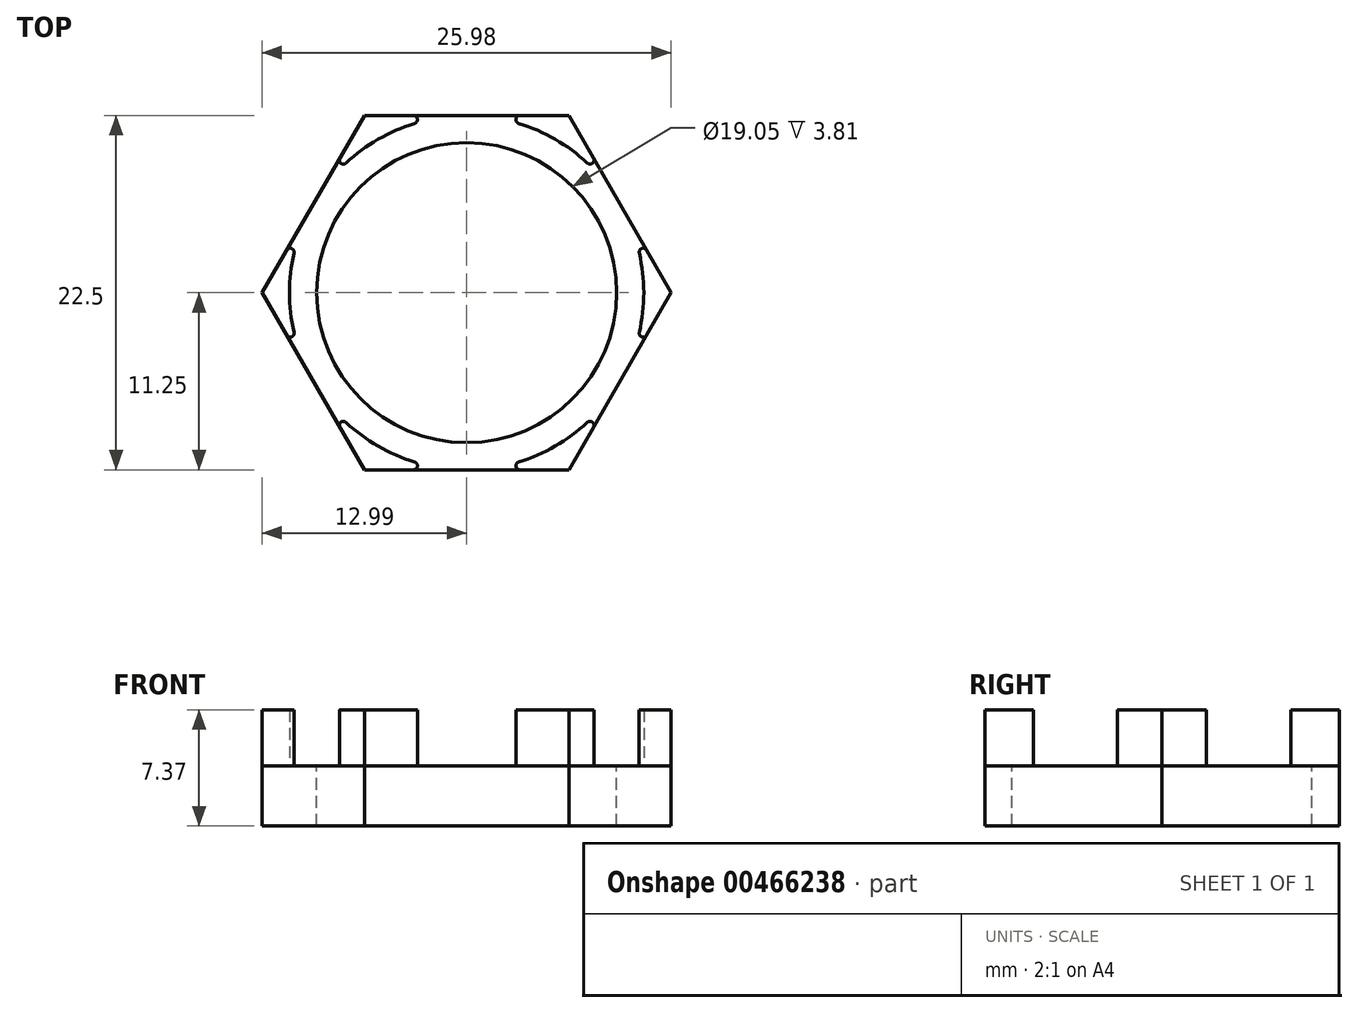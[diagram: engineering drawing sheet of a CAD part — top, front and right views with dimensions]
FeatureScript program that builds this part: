
annotation { "Feature Type Name" : "Feature", "Feature Type Description" : "" }
export const myFeature = defineFeature(function(context is Context, id is Id, definition is map)
    precondition{}
    {
        {
            var Q0;
            Q0=qCreatedBy(makeId("Top.planeOp"),FACE);
            var sketch = newSketch(context, id + "F0", { "sketchPlane" : qUnion([Q0])});
            skCircle(sketch, "E0.cCircle", {"center": v(0, 0) * mm, "radius": 11.25 * mm, "construction": true});
            skLineSegment(sketch, "E0.0", {"start": v(-6.5, 11.25) * mm, "end": v(6.5, 11.25) * mm});
            skLineSegment(sketch, "E0.1", {"start": v(6.5, 11.25) * mm, "end": v(13, 0) * mm});
            skLineSegment(sketch, "E0.2", {"start": v(13, 0) * mm, "end": v(6.5, -11.25) * mm});
            skLineSegment(sketch, "E0.3", {"start": v(6.5, -11.25) * mm, "end": v(-6.5, -11.25) * mm});
            skLineSegment(sketch, "E0.4", {"start": v(-6.5, -11.25) * mm, "end": v(-13, 0) * mm});
            skLineSegment(sketch, "E0.5", {"start": v(-13, 0) * mm, "end": v(-6.5, 11.25) * mm});
            skPoint(sketch, "E0.0.midPoint", {"position": v(0, 11.25) * mm});
            skSolve(sketch);
        }
        {
            var Q0;
            Q0=makeQuery(id+"F0.imprint","IMPRINT",FACE,{"disambiguationData":[TD([[makeQuery(id+"F0.imprint","IMPRINT",EDGE,{"derivedFrom":sQuery(id+"F0.wireOp",EDGE,"E0.0")}),-1.0]])]});
            extrude(context, id + "F1", {"entities" : qUnion([Q0]), "depth" : 3.8 * mm});
        }
        {
            var Q0;
            Q0=makeQuery(id+"F1.opExtrude","CAP_FACE",FACE,{"disambiguationData":[OSD([sQuery(id+"F0.wireOp",EDGE,"E0.0"),sQuery(id+"F0.wireOp",EDGE,"E0.1"),sQuery(id+"F0.wireOp",EDGE,"E0.2"),sQuery(id+"F0.wireOp",EDGE,"E0.3"),sQuery(id+"F0.wireOp",EDGE,"E0.4"),sQuery(id+"F0.wireOp",EDGE,"E0.5")])],"isStart":false});
            var sketch = newSketch(context, id + "F2", { "sketchPlane" : qUnion([Q0])});
            skCircle(sketch, "E1.cCircle", {"center": v(0, 0) * mm, "radius": 11.25 * mm, "construction": true});
            skLineSegment(sketch, "E1.0", {"start": v(9.74, 5.62) * mm, "end": v(13, 0) * mm});
            skLineSegment(sketch, "E1.1", {"start": v(13, 0) * mm, "end": v(9.74, -5.62) * mm});
            skPoint(sketch, "E1.0.midPoint", {"position": v(9.74, 5.62) * mm});
            skArc(sketch, "E2", {"start": v(9.74, -5.62) * mm, "mid": v(11.25, 0) * mm, "end": v(9.74, 5.62) * mm});
            skPoint(sketch, "E3.orphan", {"position": v(6.5, 11.25) * mm});
            skSolve(sketch);
        }
        {
            var Q0;
            Q0=makeQuery(id+"F2.imprint","IMPRINT",FACE,{"disambiguationData":[TD([[makeQuery(id+"F2.imprint","IMPRINT",EDGE,{"derivedFrom":sQuery(id+"F2.wireOp",EDGE,"E1.0")}),-1.0]])]});
            extrude(context, id + "F3", {"entities" : qUnion([Q0]), "depth" : 3.56 * mm});
        }
        {
            var Q0;
            Q0=makeQuery(id+"F3.opExtrude","SWEPT_EDGE",EDGE,{"disambiguationData":[OSD([sQuery(id+"F0.wireOp",EDGE,"E0.2"),sQuery(id+"F2.wireOp",EDGE,"E1.1"),sQuery(id+"F2.wireOp",EDGE,"E2")])]});
            var Q1;
            Q1=makeQuery(id+"F3.opExtrude","SWEPT_EDGE",EDGE,{"disambiguationData":[OSD([sQuery(id+"F0.wireOp",EDGE,"E0.1"),sQuery(id+"F2.wireOp",EDGE,"E1.0"),sQuery(id+"F2.wireOp",EDGE,"E2")])]});
            fillet(context, id + "F4", {"entities" : qUnion([Q0, Q1]), "radius" : 0.25 * mm, "tangentPropagation" : true, "allowEdgeOverflow" : false});
        }
        {
            var Q0;
            Q0=qCreatedBy(makeId("Front.planeOp"),FACE);
            var sketch = newSketch(context, id + "F5", { "sketchPlane" : qUnion([Q0])});
            skLineSegment(sketch, "E4", {"start": v(0, 0) * mm, "end": v(0, 39.14) * mm});
            skSolve(sketch);
        }
        {
            var Q0;
            Q0=makeQuery(id+"F3.opExtrude","SWEPT_BODY",BODY,{"disambiguationData":[OSD([sQuery(id+"F2.wireOp",EDGE,"E1.0"),sQuery(id+"F2.wireOp",EDGE,"E1.1"),sQuery(id+"F2.wireOp",EDGE,"E2")])]});
            var Q1;
            Q1=sQuery(id+"F5.wireOp",EDGE,"E4");
            circularPattern(context, id + "F6", {"entities" : qUnion([Q0]), "axis" : qUnion([Q1]), "angle" : 360 * degree, "instanceCount" : 6, "equalSpace" : true});
        }
        {
            var Q0;
            Q0=makeQuery(id+"F1.opExtrude","CAP_FACE",FACE,{"disambiguationData":[OSD([sQuery(id+"F0.wireOp",EDGE,"E0.0"),sQuery(id+"F0.wireOp",EDGE,"E0.1"),sQuery(id+"F0.wireOp",EDGE,"E0.2"),sQuery(id+"F0.wireOp",EDGE,"E0.3"),sQuery(id+"F0.wireOp",EDGE,"E0.4"),sQuery(id+"F0.wireOp",EDGE,"E0.5")])],"isStart":false});
            var sketch = newSketch(context, id + "F7", { "sketchPlane" : qUnion([Q0])});
            skSolve(sketch);
        }
        {
            var Q0;
            Q0=makeQuery(id+"F7.imprint","IMPRINT",FACE,{"disambiguationData":[TD([[makeQuery(id+"F7.imprint","IMPRINT",EDGE,{"derivedFrom":makeQuery(id+"F1.opExtrude","CAP_EDGE",EDGE,{"disambiguationData":[OSD([sQuery(id+"F0.wireOp",EDGE,"E0.0")])],"isStart":false})}),-1.0]])]});
            var sketch = newSketch(context, id + "F8", { "sketchPlane" : qUnion([Q0])});
            skCircle(sketch, "E5", {"center": v(0, 0) * mm, "radius": 9.53 * mm});
            skSolve(sketch);
        }
        {
            var Q0;
            Q0=makeQuery(id+"F8.imprint","IMPRINT",FACE,{"disambiguationData":[TD([[makeQuery(id+"F8.imprint","IMPRINT",EDGE,{"derivedFrom":sQuery(id+"F8.wireOp",EDGE,"E5")}),1.0]])]});
            extrude(context, id + "F9", {"entities" : qUnion([Q0]), "operationType" : NewBodyOperationType.REMOVE, "endBound" : BoundingType.UP_TO_NEXT, "oppositeDirection" : true, "depth" : 25.4 * mm});
        }
    });
